# Revit family: Steel-HST Top Hat-Steel & Tube-G500
name_source: partatom
category: Structural Framing
revit_build: Autodesk Revit 2017 (Build: 20170118_1100(x64)
units: mm (PartAtom-declared; Revit-internal decimal feet)

## family parameters
Always export as geometry = No
Always vertical = Yes
Cut with Voids When Loaded = No
Material for Model Behavior = Steel
OmniClass Number = 23.25.30.11.14.14
OmniClass Title = Beams
Section Shape = User Defined
Shared = No
Show family pre-cut in plan views = Yes
Structural Framing Length Roundoff = 0 mm

## types (8) — shared parameters
Assembly Code = B1020230
CBICode = 3411
CBIDescription = Structural steelwork
Coil Performance = Gauge 0.75-1.15mm; G500(MPa); 275g/m² (Zinc)
Description = Steel & Tube HST Tophat sections are an economical, lightweight, versatile and easy to use product for roof purlins, wall girts and floor joists.
Design Instruction = All the design information should be cross referenced with the current Steel & Tube Tophat Design Capacity Tables.
Design Standard = Steel & Tube’s HST Tophat profiles are designed in accordance with AS/NZS 4600:2005
Manufacturer = Steel & Tube
ManufacturerName = Steel & Tube
ManufacturerURL = http://www.steelandtube.co.nz
Material Standard = Steel & Tube’s HST Tophat profiles are manufactured from materials conforming to AS1397:2011
ModifiedIssue_ANZRS = 20160401.01 $
Perimeter = 0.00 m²/m
Principal Axes Angle = 90.00°
SpecificationDescription = Steel & Tube Purlins & Girts
SpecificationReference = 3411ST
StickSymbolEndCutBack_ANZRS = 100 mm  [stored 0.328084 ft]
Structural Material = Metal-Steel-500MPa
Torsional Modulus = 0.0 mm³
URL = http://www.steelandtube.co.nz
Uniclass2015Code = Pr_20_76_51_21
Uniclass2015Title = Cold-formed galvanized steel sections
Uniclass2015Version = 2015

## per-type parameters (varying)
| type | Centroid Horizontal | Centroid Vertical | Elastic Modulus strong axis | Elastic Modulus weak axis | Flange Thickness | Height | MassPerUnitLength_ANZRS | Moment of Inertia strong axis | Moment of Inertia weak axis | Nominal Weight | Plastic Modulus strong axis | Plastic Modulus weak axis | Profile1 | Profile2 | Profile2 Size | Section Area | SectionAreaGross_ANZRS | SectionAreaNet_ANZRS | Shear Area strong axis | Shear Area weak axis | Torsional Moment of Inertia | Warping Constant | Width |
| 60 HST Tophat 0.75 BMT | 54.3 mm | 31.7 mm | 2450.0 mm³ | 2200.0 mm³ | 0.8 mm | 60.0 mm | 1.18 kg/m | 78000.00 mm4 | 119000.00 mm4 | 1.18 kgf/m | 2450.0 mm³ | 2200.0 mm³ | Yes | No | 3 | 150.0 mm² | 150.0 mm² | 150.0 mm² | 150.0 mm² | 150.0 mm² | 28.20 mm4 | 16050000000.0 mm6 | 108.5 mm |
| 60 HST Tophat 0.95 BMT | 54.3 mm | 31.7 mm | 3090.0 mm³ | 2780.0 mm³ | 1.0 mm | 60.0 mm | 1.50 kg/m | 98000.00 mm4 | 151000.00 mm4 | 1.50 kgf/m | 3090.0 mm³ | 2780.0 mm³ | Yes | No | 3 | 190.0 mm² | 190.0 mm² | 190.0 mm² | 190.0 mm² | 190.0 mm² | 57.30 mm4 | 20330000000.0 mm6 | 108.5 mm |
| 100 HST Tophat 0.75 BMT | 81.5 mm | 55.2 mm | 6300.0 mm³ | 5390.0 mm³ | 0.8 mm | 100.0 mm | 1.93 kg/m | 338000.00 mm4 | 439000.00 mm4 | 1.93 kgf/m | 6300.0 mm³ | 5390.0 mm³ | No | Yes | 1 | 248.0 mm² | 248.0 mm² | 248.0 mm² | 248.0 mm² | 248.0 mm² | 46.50 mm4 | 238610000000.0 mm6 | 162.9 mm |
| 100 HST Tophat 0.95 BMT | 81.5 mm | 55.2 mm | 7750.0 mm³ | 6830.0 mm³ | 1.0 mm | 100.0 mm | 2.45 kg/m | 428000.00 mm4 | 556000.00 mm4 | 2.45 kgf/m | 7750.0 mm³ | 6830.0 mm³ | No | Yes | 1 | 314.0 mm² | 314.0 mm² | 314.0 mm² | 314.0 mm² | 314.0 mm² | 94.50 mm4 | 302240000000.0 mm6 | 162.9 mm |
| 120 HST Tophat 0.75 BMT | 85.0 mm | 65.6 mm | 8030.0 mm³ | 6130.0 mm³ | 0.8 mm | 120.0 mm | 2.17 kg/m | 527000.00 mm4 | 519000.00 mm4 | 2.17 kgf/m | 8030.0 mm³ | 6130.0 mm³ | No | Yes | 2 | 278.0 mm² | 278.0 mm² | 278.0 mm² | 278.0 mm² | 278.0 mm² | 52.10 mm4 | 363310000000.0 mm6 | 170.0 mm |
| 120 HST Tophat 0.95 BMT | 85.0 mm | 65.6 mm | 10160.0 mm³ | 7760.0 mm³ | 1.0 mm | 120.0 mm | 2.75 kg/m | 667000.00 mm4 | 657000.00 mm4 | 2.75 kgf/m | 10160.0 mm³ | 7760.0 mm³ | No | Yes | 2 | 352.0 mm² | 352.0 mm² | 352.0 mm² | 352.0 mm² | 352.0 mm² | 105.90 mm4 | 460200000000.0 mm6 | 170.0 mm |
| 150 HST Tophat 0.95 BMT | 91.5 mm | 81.1 mm | 14300.0 mm³ | 9600.0 mm³ | 1.0 mm | 150.0 mm | 3.21 kg/m | 1160000.00 mm4 | 878000.00 mm4 | 3.21 kgf/m | 14300.0 mm³ | 9600.0 mm³ | No | Yes | 3 | 410.0 mm² | 410.0 mm² | 410.0 mm² | 410.0 mm² | 410.0 mm² | 123.50 mm4 | 758370000000.0 mm6 | 183.0 mm |
| 150 HST Tophat 1.15 BMT | 91.5 mm | 81.1 mm | 17300.0 mm³ | 11620.0 mm³ | 1.2 mm | 150.0 mm | 3.88 kg/m | 1400000.00 mm4 | 1060000.00 mm4 | 3.88 kgf/m | 17300.0 mm³ | 11620.0 mm³ | No | Yes | 3 | 497.0 mm² | 497.0 mm² | 497.0 mm² | 497.0 mm² | 497.0 mm² | 219.10 mm4 | 918020000000.0 mm6 | 183.0 mm |

note: column(s) folded — value = type name in every type: Model

note: [stored X ft] marks values corroborated as IEEE doubles in the binary element streams (Revit-internal decimal feet)

## geometry (parser evidence)
native form markers: Sweep x4
no freeform markers — native parametric forms only
